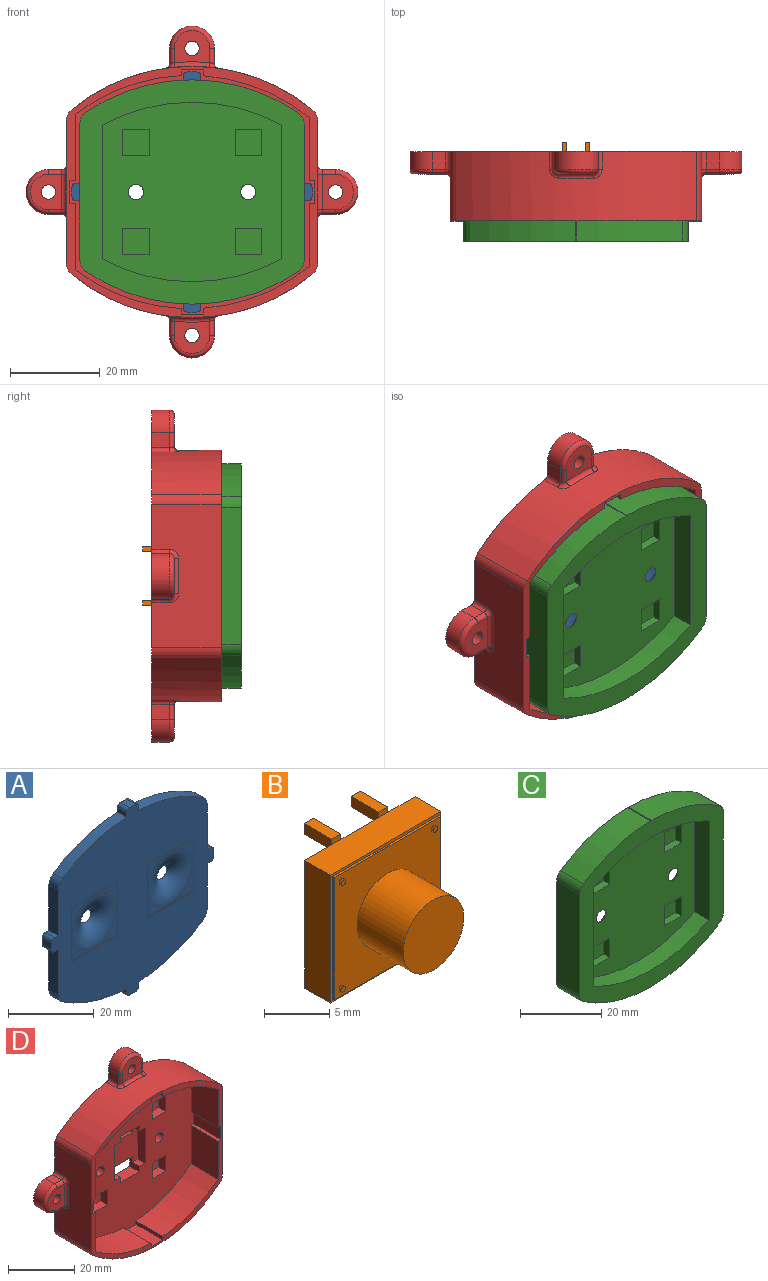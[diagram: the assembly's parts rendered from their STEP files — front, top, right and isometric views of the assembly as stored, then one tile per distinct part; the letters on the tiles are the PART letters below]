
ASSEMBLY  parts=4 mates=3
PART A: 66 faces, bbox 53.5x7.2x53.5 mm
  f0: plane 53.5x53.5mm, normal (0,-1,0), area 1719.9mm2, adj f2,f3,f4,f5,f6,f7,f8,f9
  f1: plane 53.5x53.5mm, normal (0,1,0), area 2041.5mm2, adj f2,f3,f4,f5,f6,f7,f8,f9
  f2: plane 3x1.25mm, normal (1,0,0), area 3.7mm2, adj f0,f1,f3,f61
  f3: cylinder r=42mm len=21.21mm, axis (0,1,0), area 67.8mm2, adj f0,f1,f2,f24
  f4: plane 13.06x3mm, normal (1,0,0), area 39.2mm2, adj f0,f1,f5,f24
  f5: plane 3x1.2mm, normal (0,0,-1), area 3.6mm2, adj f0,f1,f4,f59
  f6: plane 3x2mm, normal (1,0,0), area 6mm2, adj f0,f1,f58,f59
  f7: plane 3x1.2mm, normal (0,0,1), area 3.6mm2, adj f0,f1,f8,f58
  f8: plane 13.06x3mm, normal (1,0,0), area 39.2mm2, adj f0,f1,f7,f25
  f9: cylinder r=42mm len=21.21mm, axis (0,1,0), area 67.8mm2, adj f0,f1,f10,f25
  f10: plane 3x1.25mm, normal (1,0,0), area 3.7mm2, adj f0,f1,f9,f62
  f11: plane 3x2mm, normal (0,0,1), area 6mm2, adj f0,f1,f62,f63
  f12: plane 3x1.25mm, normal (-1,0,0), area 3.7mm2, adj f0,f1,f13,f63
  f13: cylinder r=42mm len=21.21mm, axis (0,1,0), area 67.8mm2, adj f0,f1,f12,f22
  f14: plane 13.06x3mm, normal (-1,0,0), area 39.2mm2, adj f0,f1,f15,f22
  f15: plane 3x1.2mm, normal (0,0,1), area 3.6mm2, adj f0,f1,f14,f64
  f16: plane 3x2mm, normal (-1,0,0), area 6mm2, adj f0,f1,f64,f65
  f17: plane 3x1.2mm, normal (0,0,-1), area 3.6mm2, adj f0,f1,f18,f65
  f18: plane 13.06x3mm, normal (-1,0,0), area 39.2mm2, adj f0,f1,f17,f23
  f19: cylinder r=42mm len=21.21mm, axis (0,1,0), area 67.8mm2, adj f0,f1,f20,f23
  f20: plane 3x1.25mm, normal (-1,0,0), area 3.7mm2, adj f0,f1,f19,f60
  f21: plane 3x2mm, normal (0,0,-1), area 6mm2, adj f0,f1,f60,f61
  f22: cylinder r=3mm len=3mm, axis (0,1,0), area 8.9mm2, adj f0,f1,f13,f14
  f23: cylinder r=3mm len=3mm, axis (0,1,0), area 8.9mm2, adj f0,f1,f18,f19
  f24: cylinder r=3mm len=3mm, axis (0,1,0), area 8.9mm2, adj f0,f1,f3,f4
  f25: cylinder r=3mm len=3mm, axis (0,1,0), area 8.9mm2, adj f0,f1,f8,f9
  f26: plane 5.8x2mm, normal (0,0,-1), area 11.6mm2, adj f1,f27,f29,f30
  f27: plane 5.8x2mm, normal (-1,0,0), area 11.6mm2, adj f1,f26,f28,f30
  f28: plane 5.8x2mm, normal (0,0,1), area 11.6mm2, adj f1,f27,f29,f30
  f29: plane 5.8x2mm, normal (1,0,0), area 11.6mm2, adj f1,f26,f28,f30
  f30: plane 5.8x5.8mm, normal (0,1,0), area 33.6mm2, adj f26,f27,f28,f29
  f31: plane 5.8x2mm, normal (0,0,-1), area 11.6mm2, adj f1,f32,f34,f35
  f32: plane 5.8x2mm, normal (-1,0,0), area 11.6mm2, adj f1,f31,f33,f35
  f33: plane 5.8x2mm, normal (0,0,1), area 11.6mm2, adj f1,f32,f34,f35
  f34: plane 5.8x2mm, normal (1,0,0), area 11.6mm2, adj f1,f31,f33,f35
  f35: plane 5.8x5.8mm, normal (0,1,0), area 33.6mm2, adj f31,f32,f33,f34
  f36: plane 5.8x2mm, normal (0,0,-1), area 11.6mm2, adj f1,f37,f39,f40
  f37: plane 5.8x2mm, normal (-1,0,0), area 11.6mm2, adj f1,f36,f38,f40
  f38: plane 5.8x2mm, normal (0,0,1), area 11.6mm2, adj f1,f37,f39,f40
  f39: plane 5.8x2mm, normal (1,0,0), area 11.6mm2, adj f1,f36,f38,f40
  f40: plane 5.8x5.8mm, normal (0,1,0), area 33.6mm2, adj f36,f37,f38,f39
  f41: plane 5.8x2mm, normal (0,0,1), area 11.6mm2, adj f1,f42,f44,f45
  f42: plane 5.8x2mm, normal (1,0,0), area 11.6mm2, adj f1,f41,f43,f45
  f43: plane 5.8x2mm, normal (0,0,-1), area 11.6mm2, adj f1,f42,f44,f45
  f44: plane 5.8x2mm, normal (-1,0,0), area 11.6mm2, adj f1,f41,f43,f45
  f45: plane 5.8x5.8mm, normal (0,1,0), area 33.6mm2, adj f41,f42,f43,f44
  f46: plane 15.4x0.2mm, normal (0,0,-1), area 3.1mm2, adj f0,f47,f49,f50
  f47: plane 15.4x0.2mm, normal (1,0,0), area 3.1mm2, adj f0,f46,f48,f50
  f48: plane 15.4x0.2mm, normal (0,0,1), area 3.1mm2, adj f0,f47,f49,f50
  f49: plane 15.4x0.2mm, normal (-1,0,0), area 3.1mm2, adj f0,f46,f48,f50
  f50: plane 15.4x15.4mm, normal (0,-1,0), area 69.7mm2, adj f46,f47,f48,f49,f57
  f51: plane 15.4x0.2mm, normal (0,0,-1), area 3.1mm2, adj f0,f52,f54,f55
  f52: plane 15.4x0.2mm, normal (1,0,0), area 3.1mm2, adj f0,f51,f53,f55
  f53: plane 15.4x0.2mm, normal (0,0,1), area 3.1mm2, adj f0,f52,f54,f55
  f54: plane 15.4x0.2mm, normal (-1,0,0), area 3.1mm2, adj f0,f51,f53,f55
  f55: plane 15.4x15.4mm, normal (0,-1,0), area 69.7mm2, adj f51,f52,f53,f54,f56
  f56: torus R=7.3mm, axis (0,-1,0), area 174.6mm2, adj f1,f55
  f57: torus R=7.3mm, axis (0,-1,0), area 174.6mm2, adj f1,f50
  f58: cylinder r=1mm len=3mm, axis (0,-1,0), area 4.7mm2, adj f0,f1,f6,f7
  f59: cylinder r=1mm len=3mm, axis (0,1,0), area 4.7mm2, adj f0,f1,f5,f6
  f60: cylinder r=1mm len=3mm, axis (0,1,0), area 4.7mm2, adj f0,f1,f20,f21
  f61: cylinder r=1mm len=3mm, axis (0,-1,0), area 4.7mm2, adj f0,f1,f2,f21
  f62: cylinder r=1mm len=3mm, axis (0,1,0), area 4.7mm2, adj f0,f1,f10,f11
  f63: cylinder r=1mm len=3mm, axis (0,-1,0), area 4.7mm2, adj f0,f1,f11,f12
  f64: cylinder r=1mm len=3mm, axis (0,-1,0), area 4.7mm2, adj f0,f1,f15,f16
  f65: cylinder r=1mm len=3mm, axis (0,1,0), area 4.7mm2, adj f0,f1,f16,f17
PART B: 45 faces, bbox 12x11x13 mm
  f0: plane 12x12mm, normal (0,1,0), area 142mm2, adj f17,f18,f19,f20,f22,f23,f24,f27
  f1: plane 11.5x11.5mm, normal (0,-1,0), area 97.3mm2, adj f2,f4,f6,f8,f10,f12,f13,f14
  f2: cylinder r=3.3mm len=6.6mm, axis (0,1,0), area 103.7mm2, adj f1,f3
  f3: plane 6.6x6.6mm, normal (0,-1,0), area 34.2mm2, adj f2
  f4: cylinder r=0.25mm len=0.5mm, axis (0,1,0), area 0.3mm2, adj f1,f5
  f5: plane 0.5x0.5mm, normal (0,-1,0), area 0.2mm2, adj f4
  f6: cylinder r=0.25mm len=0.5mm, axis (0,1,0), area 0.3mm2, adj f1,f7
  f7: plane 0.5x0.5mm, normal (0,-1,0), area 0.2mm2, adj f6
  f8: cylinder r=0.25mm len=0.5mm, axis (0,1,0), area 0.3mm2, adj f1,f9
  f9: plane 0.5x0.5mm, normal (0,-1,0), area 0.2mm2, adj f8
  f10: cylinder r=0.25mm len=0.5mm, axis (0,1,0), area 0.3mm2, adj f1,f11
  f11: plane 0.5x0.5mm, normal (0,-1,0), area 0.2mm2, adj f10
  f12: plane 11.5x0.2mm, normal (-1,0,0), area 2.3mm2, adj f1,f13,f15,f16
  f13: plane 11.5x0.2mm, normal (0,0,1), area 2.3mm2, adj f1,f12,f14,f16
  f14: plane 11.5x0.2mm, normal (1,0,0), area 2.3mm2, adj f1,f13,f15,f16
  f15: plane 11.5x0.2mm, normal (0,0,-1), area 2.3mm2, adj f1,f12,f14,f16
  f16: plane 12x12mm, normal (0,-1,0), area 11.8mm2, adj f12,f13,f14,f15,f17,f18,f19,f20
  f17: plane 12x2.8mm, normal (-1,0,0), area 33.6mm2, adj f0,f16,f18,f20
  f18: plane 12x2.8mm, normal (0,0,1), area 33.6mm2, adj f0,f16,f17,f19,f26,f32
  f19: plane 12x2.8mm, normal (1,0,0), area 33.6mm2, adj f0,f16,f18,f20
  f20: plane 12x2.8mm, normal (0,0,-1), area 33.6mm2, adj f0,f16,f17,f19,f33,f39
  f21: plane 3x1mm, normal (0,0,1), area 3mm2, adj f22,f24,f25,f26
  f22: plane 3x1mm, normal (1,0,0), area 3mm2, adj f0,f21,f23,f25,f26
  f23: plane 3x1mm, normal (0,0,-1), area 3mm2, adj f0,f22,f24,f25
  f24: plane 3x1mm, normal (-1,0,0), area 3mm2, adj f0,f21,f23,f25,f26
  f25: plane 1x1mm, normal (0,1,0), area 1mm2, adj f21,f22,f23,f24
  f26: plane 1x0.5mm, normal (0,-1,0), area 0.5mm2, adj f18,f21,f22,f24
  f27: plane 3x1mm, normal (0,0,-1), area 3mm2, adj f0,f28,f30,f31
  f28: plane 3x1mm, normal (-1,0,0), area 3mm2, adj f0,f27,f29,f31,f32
  f29: plane 3x1mm, normal (0,0,1), area 3mm2, adj f28,f30,f31,f32
  f30: plane 3x1mm, normal (1,0,0), area 3mm2, adj f0,f27,f29,f31,f32
  f31: plane 1x1mm, normal (0,1,0), area 1mm2, adj f27,f28,f29,f30
  f32: plane 1x0.5mm, normal (0,-1,0), area 0.5mm2, adj f18,f28,f29,f30
  f33: plane 1x0.5mm, normal (0,-1,0), area 0.5mm2, adj f20,f34,f35,f36
  f34: plane 3x1mm, normal (1,0,0), area 3mm2, adj f0,f33,f35,f37,f38
  f35: plane 3x1mm, normal (0,0,-1), area 3mm2, adj f33,f34,f36,f38
  f36: plane 3x1mm, normal (-1,0,0), area 3mm2, adj f0,f33,f35,f37,f38
  f37: plane 3x1mm, normal (0,0,1), area 3mm2, adj f0,f34,f36,f38
  f38: plane 1x1mm, normal (0,1,0), area 1mm2, adj f34,f35,f36,f37
  f39: plane 1x0.5mm, normal (0,-1,0), area 0.5mm2, adj f20,f40,f41,f42
  f40: plane 3x1mm, normal (1,0,0), area 3mm2, adj f0,f39,f41,f43,f44
  f41: plane 3x1mm, normal (0,0,-1), area 3mm2, adj f39,f40,f42,f44
  f42: plane 3x1mm, normal (-1,0,0), area 3mm2, adj f0,f39,f41,f43,f44
  f43: plane 3x1mm, normal (0,0,1), area 3mm2, adj f0,f40,f42,f44
  f44: plane 1x1mm, normal (0,1,0), area 1mm2, adj f40,f41,f42,f43
PART C: 49 faces, bbox 51.4x8x50 mm
  f0: plane 40x40mm, normal (0,-1,0), area 1315.6mm2, adj f8,f9,f10,f11,f27,f28,f29,f30
  f1: plane 50x50mm, normal (0,1,0), area 1761mm2, adj f2,f3,f4,f5,f6,f7,f13,f14
  f2: plane 8x0.21mm, normal (0,0,1), area 1.7mm2, adj f1,f3,f7,f12
  f3: cylinder r=42mm len=23.47mm, axis (0,1,0), area 199.4mm2, adj f1,f2,f12,f23
  f4: plane 30.48x8mm, normal (-1,0,0), area 243.8mm2, adj f1,f12,f23,f24
  f5: cylinder r=42mm len=47.38mm, axis (0,1,0), area 402.8mm2, adj f1,f12,f24,f25
  f6: plane 30.33x8mm, normal (1,0,0), area 242.7mm2, adj f1,f12,f25,f26
  f7: cylinder r=42mm len=23.7mm, axis (0,1,0), area 201.6mm2, adj f1,f2,f12,f26
  f8: cylinder r=42mm len=40mm, axis (0,1,0), area 208.5mm2, adj f0,f9,f11,f12
  f9: plane 29.86x5mm, normal (-1,0,0), area 149.3mm2, adj f0,f8,f10,f12
  f10: cylinder r=42mm len=40mm, axis (0,1,0), area 208.5mm2, adj f0,f9,f11,f12
  f11: plane 29.86x5mm, normal (1,0,0), area 149.3mm2, adj f0,f8,f10,f12
  f12: plane 50x50mm, normal (0,-1,0), area 767mm2, adj f2,f3,f4,f5,f6,f7,f8,f9
  f13: plane 15.4x0.3mm, normal (0,0,-1), area 4.6mm2, adj f1,f14,f16,f17
  f14: plane 15.4x0.3mm, normal (-1,0,0), area 4.6mm2, adj f1,f13,f15,f17
  f15: plane 15.4x0.3mm, normal (0,0,1), area 4.6mm2, adj f1,f14,f16,f17
  f16: plane 15.4x0.3mm, normal (1,0,0), area 4.6mm2, adj f1,f13,f15,f17
  f17: plane 15.4x15.4mm, normal (0,1,0), area 73.2mm2, adj f13,f14,f15,f16,f47
  f18: plane 15.4x0.3mm, normal (0,0,-1), area 4.6mm2, adj f1,f19,f21,f22
  f19: plane 15.4x0.3mm, normal (-1,0,0), area 4.6mm2, adj f1,f18,f20,f22
  f20: plane 15.4x0.3mm, normal (0,0,1), area 4.6mm2, adj f1,f19,f21,f22
  f21: plane 15.4x0.3mm, normal (1,0,0), area 4.6mm2, adj f1,f18,f20,f22
  f22: plane 15.4x15.4mm, normal (0,1,0), area 73.2mm2, adj f18,f19,f20,f21,f48
  f23: cylinder r=3mm len=8mm, axis (0,1,0), area 23.4mm2, adj f1,f3,f4,f12
  f24: cylinder r=3mm len=8mm, axis (0,1,0), area 23.3mm2, adj f1,f4,f5,f12
  f25: cylinder r=3mm len=8mm, axis (0,1,0), area 23.3mm2, adj f1,f5,f6,f12
  f26: cylinder r=3mm len=8mm, axis (0,1,0), area 23.2mm2, adj f1,f6,f7,f12
  f27: plane 5.8x2mm, normal (0,0,1), area 11.6mm2, adj f0,f28,f30,f31
  f28: plane 5.8x2mm, normal (-1,0,0), area 11.6mm2, adj f0,f27,f29,f31
  f29: plane 5.8x2mm, normal (0,0,-1), area 11.6mm2, adj f0,f28,f30,f31
  f30: plane 5.8x2mm, normal (1,0,0), area 11.6mm2, adj f0,f27,f29,f31
  f31: plane 5.8x5.8mm, normal (0,-1,0), area 33.6mm2, adj f27,f28,f29,f30
  f32: plane 5.8x2mm, normal (1,0,0), area 11.6mm2, adj f0,f33,f35,f36
  f33: plane 5.8x2mm, normal (0,0,1), area 11.6mm2, adj f0,f32,f34,f36
  f34: plane 5.8x2mm, normal (-1,0,0), area 11.6mm2, adj f0,f33,f35,f36
  f35: plane 5.8x2mm, normal (0,0,-1), area 11.6mm2, adj f0,f32,f34,f36
  f36: plane 5.8x5.8mm, normal (0,-1,0), area 33.6mm2, adj f32,f33,f34,f35
  f37: plane 5.8x2mm, normal (1,0,0), area 11.6mm2, adj f0,f38,f40,f41
  f38: plane 5.8x2mm, normal (0,0,1), area 11.6mm2, adj f0,f37,f39,f41
  f39: plane 5.8x2mm, normal (-1,0,0), area 11.6mm2, adj f0,f38,f40,f41
  f40: plane 5.8x2mm, normal (0,0,-1), area 11.6mm2, adj f0,f37,f39,f41
  f41: plane 5.8x5.8mm, normal (0,-1,0), area 33.6mm2, adj f37,f38,f39,f40
  f42: plane 5.8x2mm, normal (0,0,1), area 11.6mm2, adj f0,f43,f45,f46
  f43: plane 5.8x2mm, normal (-1,0,0), area 11.6mm2, adj f0,f42,f44,f46
  f44: plane 5.8x2mm, normal (0,0,-1), area 11.6mm2, adj f0,f43,f45,f46
  f45: plane 5.8x2mm, normal (1,0,0), area 11.6mm2, adj f0,f42,f44,f46
  f46: plane 5.8x5.8mm, normal (0,-1,0), area 33.6mm2, adj f42,f43,f44,f45
  f47: torus R=7.22mm, axis (0,1,0), area 170.1mm2, adj f0,f17
  f48: torus R=7.22mm, axis (0,1,0), area 170.1mm2, adj f0,f22
PART D: 121 faces, bbox 74.8x15.5x74.8 mm
  f0: cylinder r=42mm len=53.85mm, axis (0,1,0), area 837.1mm2, adj f6,f16,f65,f66,f97,f99,f101,f103
  f1: cylinder r=42mm len=53.85mm, axis (0,1,0), area 837.1mm2, adj f6,f16,f67,f68,f113,f115,f117,f119
  f2: plane 14.05x11.5mm, normal (-1,0,0), area 161.6mm2, adj f5,f6,f7,f57
  f3: plane 14.81x11.5mm, normal (1,0,0), area 170.3mm2, adj f6,f7,f50,f59
  f4: cylinder r=42mm len=23.57mm, axis (0,1,0), area 293.3mm2, adj f6,f7,f51,f62
  f5: cylinder r=42mm len=23.57mm, axis (0,1,0), area 296.3mm2, adj f2,f6,f7,f55
  f6: plane 56x56mm, normal (0,-1,0), area 322.5mm2, adj f0,f1,f2,f3,f4,f5,f12,f13
  f7: plane 54.54x54.41mm, normal (0,-1,0), area 2082.3mm2, adj f2,f3,f4,f5,f9,f11,f14,f15
  f8: plane 8x1mm, normal (0,0,-1), area 8mm2, adj f16,f17,f19,f27
  f9: plane 4x4mm, normal (1,0,0), area 10mm2, adj f7,f10,f16,f20,f24,f27
  f10: plane 8x1mm, normal (0,0,1), area 8mm2, adj f9,f11,f16,f27
  f11: plane 4x4mm, normal (-1,0,0), area 10mm2, adj f7,f10,f16,f20,f23,f27
  f12: plane 31.87x15.5mm, normal (-1,0,0), area 423.6mm2, adj f6,f16,f65,f68,f105,f107,f109,f111
  f13: plane 31.87x15.5mm, normal (1,0,0), area 423.6mm2, adj f6,f16,f66,f67,f89,f91,f93,f95
  f14: cylinder r=1.7mm len=4mm, axis (0,1,0), area 42.7mm2, adj f7,f16
  f15: cylinder r=1.7mm len=4mm, axis (0,1,0), area 42.7mm2, adj f7,f16
  f16: plane 74x74mm, normal (0,1,0), area 2964.7mm2, adj f0,f1,f8,f9,f10,f11,f12,f13
  f17: plane 4x4mm, normal (1,0,0), area 10mm2, adj f7,f8,f16,f18,f26,f27
  f18: plane 8x4mm, normal (0,0,1), area 32mm2, adj f7,f16,f17,f19
  f19: plane 4x4mm, normal (-1,0,0), area 10mm2, adj f7,f8,f16,f18,f21,f27
  f20: plane 8x4mm, normal (0,0,-1), area 32mm2, adj f7,f9,f11,f16
  f21: plane 3x2.5mm, normal (0,0,1), area 7.5mm2, adj f7,f19,f22,f27
  f22: plane 13x3mm, normal (-1,0,0), area 39mm2, adj f7,f21,f23,f27
  f23: plane 3x2.5mm, normal (0,0,-1), area 7.5mm2, adj f7,f11,f22,f27
  f24: plane 3x2.5mm, normal (0,0,-1), area 7.5mm2, adj f7,f9,f25,f27
  f25: plane 13x3mm, normal (1,0,0), area 39mm2, adj f7,f24,f26,f27
  f26: plane 3x2.5mm, normal (0,0,1), area 7.5mm2, adj f7,f17,f25,f27
  f27: plane 13x13mm, normal (0,-1,0), area 137mm2, adj f8,f9,f10,f11,f17,f19,f21,f22
  f28: plane 5.8x3mm, normal (0,0,-1), area 17.4mm2, adj f7,f29,f31,f32
  f29: plane 5.8x3mm, normal (1,0,0), area 17.4mm2, adj f7,f28,f30,f32
  f30: plane 5.8x3mm, normal (0,0,1), area 17.4mm2, adj f7,f29,f31,f32
  f31: plane 5.8x3mm, normal (-1,0,0), area 17.4mm2, adj f7,f28,f30,f32
  f32: plane 5.8x5.8mm, normal (0,-1,0), area 33.6mm2, adj f28,f29,f30,f31
  f33: plane 5.8x3mm, normal (-1,0,0), area 17.4mm2, adj f7,f34,f36,f37
  f34: plane 5.8x3mm, normal (0,0,-1), area 17.4mm2, adj f7,f33,f35,f37
  f35: plane 5.8x3mm, normal (1,0,0), area 17.4mm2, adj f7,f34,f36,f37
  f36: plane 5.8x3mm, normal (0,0,1), area 17.4mm2, adj f7,f33,f35,f37
  f37: plane 5.8x5.8mm, normal (0,-1,0), area 33.6mm2, adj f33,f34,f35,f36
  f38: plane 5.8x3mm, normal (1,0,0), area 17.4mm2, adj f7,f39,f41,f42
  f39: plane 5.8x3mm, normal (0,0,1), area 17.4mm2, adj f7,f38,f40,f42
  f40: plane 5.8x3mm, normal (-1,0,0), area 17.4mm2, adj f7,f39,f41,f42
  f41: plane 5.8x3mm, normal (0,0,-1), area 17.4mm2, adj f7,f38,f40,f42
  f42: plane 5.8x5.8mm, normal (0,-1,0), area 33.6mm2, adj f38,f39,f40,f41
  f43: plane 5.8x3mm, normal (-1,0,0), area 17.4mm2, adj f7,f44,f46,f47
  f44: plane 5.8x3mm, normal (0,0,-1), area 17.4mm2, adj f7,f43,f45,f47
  f45: plane 5.8x3mm, normal (1,0,0), area 17.4mm2, adj f7,f44,f46,f47
  f46: plane 5.8x3mm, normal (0,0,1), area 17.4mm2, adj f7,f43,f45,f47
  f47: plane 5.8x5.8mm, normal (0,-1,0), area 33.6mm2, adj f43,f44,f45,f46
  f48: cylinder r=42mm len=23.57mm, axis (0,1,0), area 296.2mm2, adj f6,f7,f49,f63
  f49: plane 14.07x11.5mm, normal (-1,0,0), area 161.8mm2, adj f6,f7,f48,f56
  f50: cylinder r=42mm len=23.48mm, axis (0,1,0), area 292.2mm2, adj f3,f6,f7,f52
  f51: plane 14.81x11.5mm, normal (1,0,0), area 170.3mm2, adj f4,f6,f7,f60
  f52: plane 11.5x0.09mm, normal (0.49,0,0.87), area 1.2mm2, adj f6,f7,f50,f53
  f53: plane 11.5x1.2mm, normal (1,0,0), area 13.8mm2, adj f6,f7,f52,f54
  f54: plane 11.5x5mm, normal (0,0,1), area 57.5mm2, adj f6,f7,f53,f55
  f55: plane 11.5x1.3mm, normal (-1,0,0), area 15mm2, adj f5,f6,f7,f54
  f56: plane 11.5x1.2mm, normal (0,0,-1), area 13.8mm2, adj f6,f7,f49,f58
  f57: plane 11.5x1.2mm, normal (0,0,1), area 13.8mm2, adj f2,f6,f7,f58
  f58: plane 11.5x5mm, normal (-1,0,0), area 57.5mm2, adj f6,f7,f56,f57
  f59: plane 11.5x1.2mm, normal (0,0,1), area 13.8mm2, adj f3,f6,f7,f61
  f60: plane 11.5x1.2mm, normal (0,0,-1), area 13.8mm2, adj f6,f7,f51,f61
  f61: plane 11.5x5mm, normal (1,0,0), area 57.5mm2, adj f6,f7,f59,f60
  f62: plane 11.5x1.25mm, normal (1,0,0), area 14.3mm2, adj f4,f6,f7,f64
  f63: plane 11.5x1.3mm, normal (-1,0,0), area 15mm2, adj f6,f7,f48,f64
  f64: plane 11.5x5mm, normal (0,0,-1), area 57.5mm2, adj f6,f7,f62,f63
  f65: cylinder r=3mm len=15.5mm, axis (0,1,0), area 40.7mm2, adj f0,f6,f12,f16
  f66: cylinder r=3mm len=15.5mm, axis (0,1,0), area 40.7mm2, adj f0,f6,f13,f16
  f67: cylinder r=3mm len=15.5mm, axis (0,1,0), area 40.7mm2, adj f1,f6,f13,f16
  f68: cylinder r=3mm len=15.5mm, axis (0,1,0), area 40.7mm2, adj f1,f6,f12,f16
  f69: plane 4x3mm, normal (0,0,1), area 12mm2, adj f16,f70,f110,f112
  f70: cylinder r=5mm len=10mm, axis (0,1,0), area 62.8mm2, adj f16,f69,f71,f108
  f71: plane 4x3mm, normal (0,0,-1), area 12mm2, adj f16,f70,f105,f106
  f72: cylinder r=1.6mm len=5mm, axis (0,1,0), area 50.3mm2, adj f16,f73
  f73: plane 8x7mm, normal (0,-1,0), area 41.1mm2, adj f72,f106,f108,f109,f110
  f74: plane 4x3mm, normal (0,0,-1), area 12mm2, adj f16,f75,f94,f96
  f75: cylinder r=5mm len=10mm, axis (0,1,0), area 62.8mm2, adj f16,f74,f76,f92
  f76: plane 4x3mm, normal (0,0,1), area 12mm2, adj f16,f75,f89,f90
  f77: cylinder r=1.6mm len=5mm, axis (0,1,0), area 50.3mm2, adj f16,f78
  f78: plane 8x7mm, normal (0,-1,0), area 41.1mm2, adj f77,f90,f92,f93,f94
  f79: plane 4x3.42mm, normal (1,0,0), area 13.7mm2, adj f16,f80,f118,f120
  f80: cylinder r=5mm len=10mm, axis (0,1,0), area 62.8mm2, adj f16,f79,f81,f116
  f81: plane 4x3.42mm, normal (-1,0,0), area 13.7mm2, adj f16,f80,f113,f114
  f82: cylinder r=1.6mm len=5mm, axis (0,1,0), area 50.3mm2, adj f16,f83
  f83: plane 8x7.19mm, normal (0,-1,0), area 41.6mm2, adj f82,f114,f116,f117,f118
  f84: plane 4x3.42mm, normal (-1,0,0), area 13.7mm2, adj f16,f85,f102,f104
  f85: cylinder r=5mm len=10mm, axis (0,1,0), area 62.8mm2, adj f16,f84,f86,f100
  f86: plane 4x3.42mm, normal (1,0,0), area 13.7mm2, adj f16,f85,f97,f98
  f87: cylinder r=1.6mm len=5mm, axis (0,1,0), area 50.3mm2, adj f16,f88
  f88: plane 8x7.19mm, normal (0,-1,0), area 41.6mm2, adj f87,f98,f100,f101,f102
  f89: cylinder r=1mm len=4mm, axis (0,1,0), area 6.3mm2, adj f13,f16,f76,f91
  f90: cylinder r=1mm len=3mm, axis (1,0,0), area 4.7mm2, adj f76,f78,f91,f92
  f91: torus R=2mm, axis (1,0,0), area 3.4mm2, adj f13,f89,f90,f93
  f92: torus R=4mm, axis (0,-1,0), area 22.9mm2, adj f75,f78,f90,f94
  f93: cylinder r=1mm len=8mm, axis (0,0,1), area 12.6mm2, adj f13,f78,f91,f95
  f94: cylinder r=1mm len=3mm, axis (-1,0,0), area 4.7mm2, adj f74,f78,f92,f95
  f95: torus R=2mm, axis (1,0,0), area 3.4mm2, adj f13,f93,f94,f96
  f96: cylinder r=1mm len=4mm, axis (0,-1,0), area 6.3mm2, adj f13,f16,f74,f95
  f97: cylinder r=1mm len=4mm, axis (0,1,0), area 5.7mm2, adj f0,f16,f86,f99
  f98: cylinder r=1mm len=3.42mm, axis (0,0,-1), area 5.2mm2, adj f86,f88,f99,f100
  f99: bspline ~2.39x2.35mm, area 3.2mm2, adj f0,f97,f98,f101
  f100: torus R=4mm, axis (0,-1,0), area 22.9mm2, adj f85,f88,f98,f102
  f101: torus R=43mm, axis (0,-1,0), area 12.4mm2, adj f0,f88,f99,f103
  f102: cylinder r=1mm len=3.42mm, axis (0,0,1), area 5.2mm2, adj f84,f88,f100,f103
  f103: bspline ~2.45x2.28mm, area 3.2mm2, adj f0,f101,f102,f104
  f104: cylinder r=1mm len=4mm, axis (0,1,0), area 5.7mm2, adj f0,f16,f84,f103
  f105: cylinder r=1mm len=4mm, axis (0,-1,0), area 6.3mm2, adj f12,f16,f71,f107
  f106: cylinder r=1mm len=3mm, axis (-1,0,0), area 4.7mm2, adj f71,f73,f107,f108
  f107: torus R=2mm, axis (1,0,0), area 3.4mm2, adj f12,f105,f106,f109
  f108: torus R=4mm, axis (0,-1,0), area 22.9mm2, adj f70,f73,f106,f110
  f109: cylinder r=1mm len=8mm, axis (0,0,-1), area 12.6mm2, adj f12,f73,f107,f111
  f110: cylinder r=1mm len=3mm, axis (1,0,0), area 4.7mm2, adj f69,f73,f108,f111
  f111: torus R=2mm, axis (1,0,0), area 3.4mm2, adj f12,f109,f110,f112
  f112: cylinder r=1mm len=4mm, axis (0,1,0), area 6.3mm2, adj f12,f16,f69,f111
  f113: cylinder r=1mm len=4mm, axis (0,1,0), area 5.7mm2, adj f1,f16,f81,f115
  f114: cylinder r=1mm len=3.42mm, axis (0,0,1), area 5.2mm2, adj f81,f83,f115,f116
  f115: bspline ~2.39x2.35mm, area 3.2mm2, adj f1,f113,f114,f117
  f116: torus R=4mm, axis (0,-1,0), area 22.9mm2, adj f80,f83,f114,f118
  f117: torus R=43mm, axis (0,-1,0), area 12.4mm2, adj f1,f83,f115,f119
  f118: cylinder r=1mm len=3.42mm, axis (0,0,-1), area 5.2mm2, adj f79,f83,f116,f119
  f119: bspline ~2.45x2.28mm, area 3.2mm2, adj f1,f117,f118,f120
  f120: cylinder r=1mm len=4mm, axis (0,1,0), area 5.7mm2, adj f1,f16,f79,f119
PLACE A t=(-59.87,-30.8,8.1)mm
PLACE B t=(-117.49,-22.8,27.49)mm
PLACE C t=(-111.9,-33.8,39.39)mm
PLACE D t=(-75.1,-21.8,39.05)mm
MATE fastened A.f0 <-> C.f1  axis (0,-1,0) through (-106.37,-33.8,40.06)mm
MATE fastened D.f27 <-> B.f2  axis (0,-1,0) through (-106.37,-22.8,40.06)mm
MATE fastened A.f1 <-> B.f2  axis (0,1,0) through (-106.37,-30.8,40.06)mm
